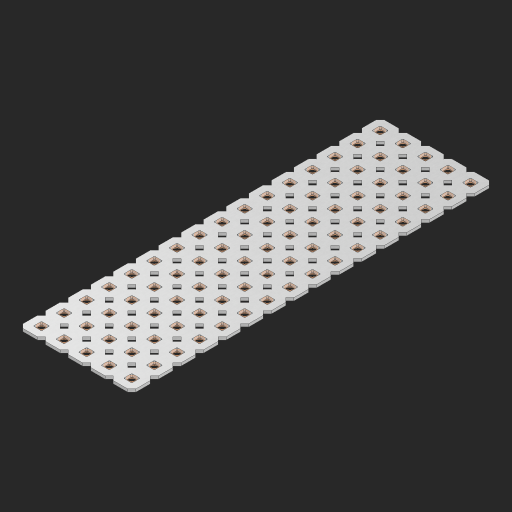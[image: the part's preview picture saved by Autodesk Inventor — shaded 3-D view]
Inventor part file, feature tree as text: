
AUTODESK INVENTOR PART (.ipt)
format: ipt  version: 2023 (Build 270158000, 158)  size: 1,211,904 bytes
history: native  units: in
note: dims shown in document units (in); Inventor stores cm internally (conversion verified against a paired STEP export)
features: other x81, extrude x79, sketch x2, pattern_linear x1
ambient origin geometry x8: Origin, YZ Plane, XZ Plane, XY Plane, X Axis, Y Axis, Z Axis, Center Point
bodies: Solid1 (feature_tree), Body (feature_tree)
feature tree (163):
  pattern_linear  "Rectangular Pattern1"  Spacing1=0.09in  [1 undecoded]
  sketch  "Sketch1"  dims[d1=0.5in]
  sketch  "Sketch2"  dims[d2=0.182in d3=0.09in d4=0.09in d5=0.09in d6=0.09in d7=0.09in d8=0.09in d9=0.09in d10=0.09in d11=0.02in d13=0.0in d14=0.172in d15=0.0625in d16=0.0in d19=0.5in d22=0.5in]
  other  "Srf1"
  other  "Srf126"
  other  "Srf127"
  other  "Srf128"
  other  "Srf129"
  other  "Srf130"
  other  "Srf131"
  other  "Srf250"
  other  "Srf251"
  other  "Srf252"
  other  "Srf253"
  other  "Srf254"
  other  "Srf255"
  other  "Srf256"
  other  "Srf257"
  other  "Srf258"
  other  "Srf268"
  other  "Srf269"
  other  "Srf270"
  other  "Srf271"
  other  "Srf272"
  other  "Srf273"
  other  "Srf274"
  other  "Srf275"
  other  "Srf276"
  other  "Srf277"
  other  "Srf278"
  other  "Srf279"
  other  "Srf280"
  other  "Srf281"
  other  "Srf282"
  other  "Srf283"
  other  "Srf293"
  other  "Srf294"
  other  "Srf295"
  other  "Srf296"
  other  "Srf297"
  other  "Srf298"
  other  "Srf299"
  other  "Srf300"
  other  "Srf301"
  other  "Srf302"
  other  "Srf303"
  other  "Srf304"
  other  "Srf305"
  other  "Srf306"
  other  "Srf307"
  other  "Srf308"
  other  "Srf318"
  other  "Srf319"
  other  "Srf320"
  other  "Srf321"
  other  "Srf322"
  other  "Srf323"
  other  "Srf324"
  other  "Srf325"
  other  "Srf326"
  other  "Srf327"
  other  "Srf328"
  other  "Srf329"
  other  "Srf330"
  other  "Srf331"
  other  "Srf332"
  other  "Srf333"
  other  "Srf343"
  other  "Srf344"
  other  "Srf345"
  other  "Srf346"
  other  "Srf347"
  other  "Srf348"
  other  "Srf349"
  other  "Srf350"
  other  "Srf351"
  other  "Srf352"
  other  "Srf353"
  other  "Srf354"
  other  "Srf355"
  other  "Srf356"
  other  "Srf357"
  other  "Srf358"
  other  "Circle"
  extrude  "ExtrusionSrf126"  Depth=0.09in
  extrude  "ExtrusionSrf127"  Depth=0.09in
  extrude  "ExtrusionSrf128"  Depth=0.09in
  extrude  "ExtrusionSrf129"  Depth=0.09in
  extrude  "ExtrusionSrf130"  Depth=0.09in
  extrude  "ExtrusionSrf131"  Depth=0.09in
  extrude  "ExtrusionSrf250"  Depth=0.09in
  extrude  "ExtrusionSrf251"  Depth=0.02in
  extrude  "ExtrusionSrf252"  TaperAngle=0.0deg  [1 undecoded]
  extrude  "ExtrusionSrf253"  Depth=0.5in
  extrude  "ExtrusionSrf254"  Depth=0.0625in TaperAngle=0.0deg
  extrude  "ExtrusionSrf255"  Depth=0.5in
  extrude  "ExtrusionSrf256"  Depth=0.5in
  extrude  "ExtrusionSrf257"  [1 undecoded]
  extrude  "ExtrusionSrf258"  [1 undecoded]
  extrude  "ExtrusionSrf268"  [1 undecoded]
  extrude  "ExtrusionSrf269"  [1 undecoded]
  extrude  "ExtrusionSrf270"  [1 undecoded]
  extrude  "ExtrusionSrf271"  [1 undecoded]
  extrude  "ExtrusionSrf272"  [1 undecoded]
  extrude  "ExtrusionSrf273"  [1 undecoded]
  extrude  "ExtrusionSrf274"  [1 undecoded]
  extrude  "ExtrusionSrf275"  [1 undecoded]
  extrude  "ExtrusionSrf276"  [1 undecoded]
  extrude  "ExtrusionSrf277"  [1 undecoded]
  extrude  "ExtrusionSrf278"  [1 undecoded]
  extrude  "ExtrusionSrf279"  [1 undecoded]
  extrude  "ExtrusionSrf280"  [1 undecoded]
  extrude  "ExtrusionSrf281"  [1 undecoded]
  extrude  "ExtrusionSrf282"  [1 undecoded]
  extrude  "ExtrusionSrf283"  [1 undecoded]
  extrude  "ExtrusionSrf293"  [1 undecoded]
  extrude  "ExtrusionSrf294"  [1 undecoded]
  extrude  "ExtrusionSrf295"  [1 undecoded]
  extrude  "ExtrusionSrf296"  [1 undecoded]
  extrude  "ExtrusionSrf297"  [1 undecoded]
  extrude  "ExtrusionSrf298"  [1 undecoded]
  extrude  "ExtrusionSrf299"  [1 undecoded]
  extrude  "ExtrusionSrf300"  [1 undecoded]
  extrude  "ExtrusionSrf301"  [1 undecoded]
  extrude  "ExtrusionSrf302"  [1 undecoded]
  extrude  "ExtrusionSrf303"  [1 undecoded]
  extrude  "ExtrusionSrf304"  [1 undecoded]
  extrude  "ExtrusionSrf305"  [1 undecoded]
  extrude  "ExtrusionSrf306"  [1 undecoded]
  extrude  "ExtrusionSrf307"  [1 undecoded]
  extrude  "ExtrusionSrf308"  [1 undecoded]
  extrude  "ExtrusionSrf318"  [1 undecoded]
  extrude  "ExtrusionSrf319"  [1 undecoded]
  extrude  "ExtrusionSrf320"  [1 undecoded]
  extrude  "ExtrusionSrf321"  [1 undecoded]
  extrude  "ExtrusionSrf322"  [1 undecoded]
  extrude  "ExtrusionSrf323"  [1 undecoded]
  extrude  "ExtrusionSrf324"  [1 undecoded]
  extrude  "ExtrusionSrf325"  [1 undecoded]
  extrude  "ExtrusionSrf326"  [1 undecoded]
  extrude  "ExtrusionSrf327"  [1 undecoded]
  extrude  "ExtrusionSrf328"  [1 undecoded]
  extrude  "ExtrusionSrf329"  [1 undecoded]
  extrude  "ExtrusionSrf330"  [1 undecoded]
  extrude  "ExtrusionSrf331"  [1 undecoded]
  extrude  "ExtrusionSrf332"  [1 undecoded]
  extrude  "ExtrusionSrf333"  [1 undecoded]
  extrude  "ExtrusionSrf343"  [1 undecoded]
  extrude  "ExtrusionSrf344"  [1 undecoded]
  extrude  "ExtrusionSrf345"  [1 undecoded]
  extrude  "ExtrusionSrf346"  [1 undecoded]
  extrude  "ExtrusionSrf347"  [1 undecoded]
  extrude  "ExtrusionSrf348"  [1 undecoded]
  extrude  "ExtrusionSrf349"  [1 undecoded]
  extrude  "ExtrusionSrf350"  [1 undecoded]
  extrude  "ExtrusionSrf351"  [1 undecoded]
  extrude  "ExtrusionSrf352"  [1 undecoded]
  extrude  "ExtrusionSrf353"  [1 undecoded]
  extrude  "ExtrusionSrf354"  [1 undecoded]
  extrude  "ExtrusionSrf355"  [1 undecoded]
  extrude  "ExtrusionSrf356"  [1 undecoded]
  extrude  "ExtrusionSrf357"  [1 undecoded]
  extrude  "ExtrusionSrf358"  [1 undecoded]
note: 68 required parameter values undecoded (feature->parameter linkage not recoverable at this tier; creation-order binding heuristic only, values carry confidence <= 0.55)
